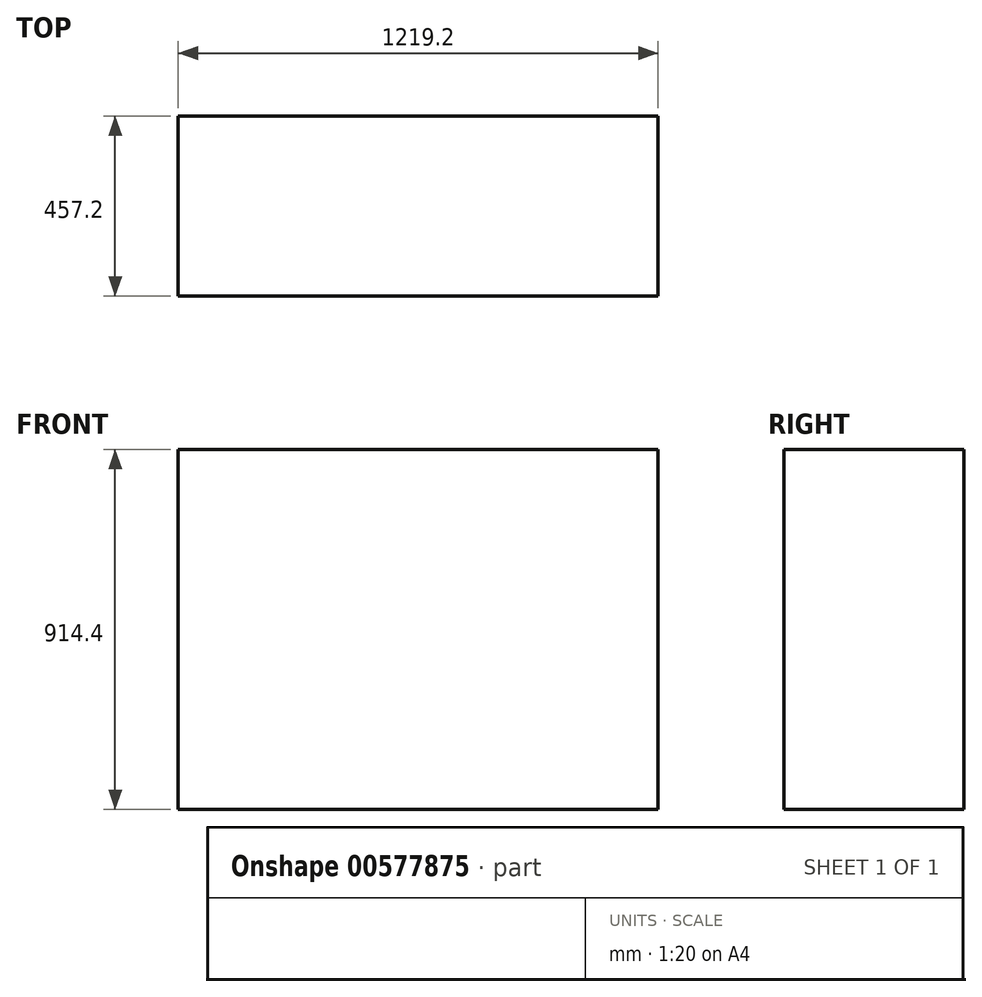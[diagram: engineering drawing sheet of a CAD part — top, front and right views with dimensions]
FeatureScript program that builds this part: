
annotation { "Feature Type Name" : "Feature", "Feature Type Description" : "" }
export const myFeature = defineFeature(function(context is Context, id is Id, definition is map)
    precondition{}
    {
        {
            var Q0;
            Q0=qCreatedBy(makeId("Top.planeOp"),FACE);
            var sketch = newSketch(context, id + "F0", { "sketchPlane" : qUnion([Q0])});
            skLineSegment(sketch, "E0.bottom", {"start": v(609.6, 228.6) * mm, "end": v(-609.6, 228.6) * mm});
            skLineSegment(sketch, "E0.top", {"start": v(609.6, -228.6) * mm, "end": v(-609.6, -228.6) * mm});
            skLineSegment(sketch, "E0.left", {"start": v(609.6, 228.6) * mm, "end": v(609.6, -228.6) * mm});
            skLineSegment(sketch, "E0.right", {"start": v(-609.6, 228.6) * mm, "end": v(-609.6, -228.6) * mm});
            skPoint(sketch, "E0.middle", {"position": v(0, 0) * mm});
            skSolve(sketch);
        }
        {
            var Q0;
            Q0=makeQuery(id+"F0.imprint","IMPRINT",FACE,{"disambiguationData":[TD([[makeQuery(id+"F0.imprint","IMPRINT",EDGE,{"derivedFrom":sQuery(id+"F0.wireOp",EDGE,"E0.bottom")}),1.0]])]});
            extrude(context, id + "F1", {"entities" : qUnion([Q0]), "depth" : 914.4 * mm, "offsetDistance" : 25.4 * mm});
        }
    });
